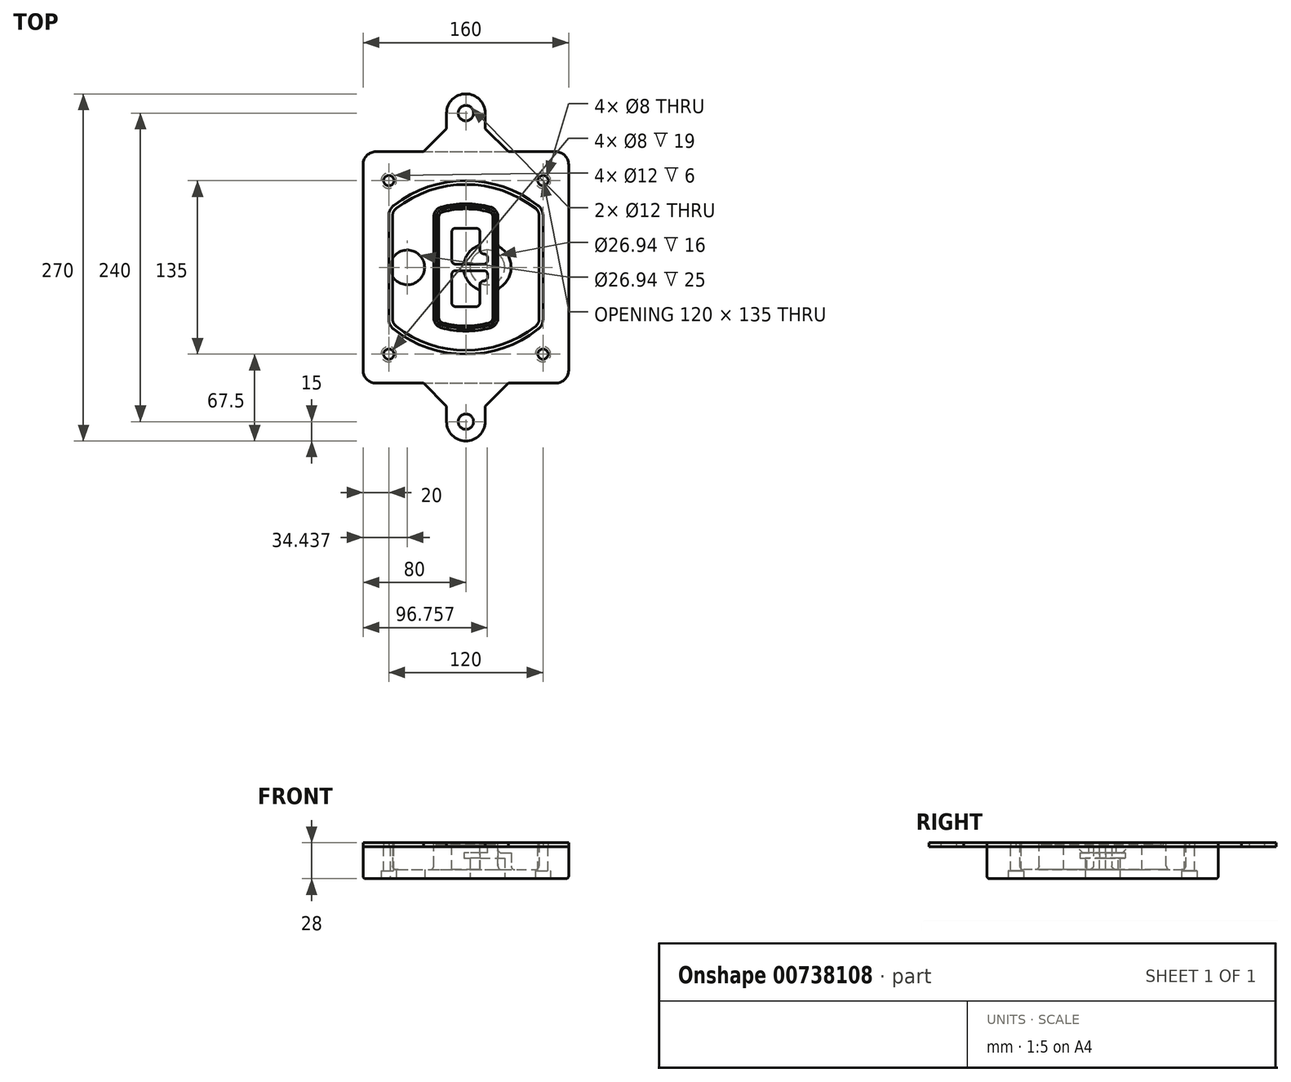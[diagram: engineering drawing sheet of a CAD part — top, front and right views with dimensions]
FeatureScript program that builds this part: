
annotation { "Feature Type Name" : "Feature", "Feature Type Description" : "" }
export const myFeature = defineFeature(function(context is Context, id is Id, definition is map)
    precondition{}
    {
        {
            var Q0;
            Q0=qCreatedBy(makeId("Top.planeOp"),FACE);
            var sketch = newSketch(context, id + "F0", { "sketchPlane" : qUnion([Q0])});
            skPoint(sketch, "E0.rect.middle", {"position": v(0, 0) * mm});
            skLineSegment(sketch, "E1.bottom", {"start": v(-70, -90) * mm, "end": v(70, -90) * mm});
            skLineSegment(sketch, "E1.top", {"start": v(-70, 90) * mm, "end": v(70, 90) * mm});
            skLineSegment(sketch, "E1.left", {"start": v(-80, -80) * mm, "end": v(-80, 80) * mm});
            skLineSegment(sketch, "E1.right", {"start": v(80, -80) * mm, "end": v(80, 80) * mm});
            skLineSegment(sketch, "E2", {"start": v(-80, 90) * mm, "end": v(80, -90) * mm, "construction": true});
            skLineSegment(sketch, "E3", {"start": v(80, 90) * mm, "end": v(-80, -90) * mm, "construction": true});
            skCircle(sketch, "E4", {"center": v(-60, 67.5) * mm, "radius": 4 * mm});
            skCircle(sketch, "E5", {"center": v(60, 67.5) * mm, "radius": 4 * mm});
            skCircle(sketch, "E6", {"center": v(60, -67.5) * mm, "radius": 4 * mm});
            skCircle(sketch, "E7", {"center": v(-60, -67.5) * mm, "radius": 4 * mm});
            skLineSegment(sketch, "E8", {"start": v(-60, 67.5) * mm, "end": v(60, 67.5) * mm, "construction": true});
            skLineSegment(sketch, "E9", {"start": v(60, 67.5) * mm, "end": v(60, -67.5) * mm, "construction": true});
            skLineSegment(sketch, "E10", {"start": v(60, -67.5) * mm, "end": v(-60, -67.5) * mm, "construction": true});
            skLineSegment(sketch, "E11", {"start": v(-60, -67.5) * mm, "end": v(-60, 67.5) * mm, "construction": true});
            skLineSegment(sketch, "E12", {"start": v(-60, 40.3) * mm, "end": v(-60, -40.3) * mm});
            skLineSegment(sketch, "E13", {"start": v(60, 40.3) * mm, "end": v(60, -40.3) * mm});
            skArc(sketch, "E14", {"start": v(56.15, 48.18) * mm, "mid": v(0, 67.5) * mm, "end": v(-56.15, 48.18) * mm});
            skArc(sketch, "E15", {"start": v(-56.15, -48.18) * mm, "mid": v(0, -67.5) * mm, "end": v(56.15, -48.18) * mm});
            skLineSegment(sketch, "E16", {"start": v(-60, 0) * mm, "end": v(60, 0) * mm, "construction": true});
            skPoint(sketch, "E17.visualSharp", {"position": v(-60, -45) * mm});
            skArc(sketch, "E17.filletArc", {"start": v(-60, -40.3) * mm, "mid": v(-58.99, -44.68) * mm, "end": v(-56.15, -48.18) * mm});
            skPoint(sketch, "E18.visualSharp", {"position": v(-60, 45) * mm});
            skArc(sketch, "E18.filletArc", {"start": v(-56.15, 48.18) * mm, "mid": v(-58.99, 44.68) * mm, "end": v(-60, 40.3) * mm});
            skPoint(sketch, "E19.visualSharp", {"position": v(60, 45) * mm});
            skArc(sketch, "E19.filletArc", {"start": v(60, 40.3) * mm, "mid": v(58.99, 44.68) * mm, "end": v(56.15, 48.18) * mm});
            skPoint(sketch, "E20.visualSharp", {"position": v(60, -45) * mm});
            skArc(sketch, "E20.filletArc", {"start": v(56.15, -48.18) * mm, "mid": v(58.99, -44.68) * mm, "end": v(60, -40.3) * mm});
            skPoint(sketch, "E21.visualSharp", {"position": v(-80, 90) * mm});
            skArc(sketch, "E21.filletArc", {"start": v(-70, 90) * mm, "mid": v(-77.07, 87.07) * mm, "end": v(-80, 80) * mm});
            skPoint(sketch, "E22.visualSharp", {"position": v(80, 90) * mm});
            skArc(sketch, "E22.filletArc", {"start": v(80, 80) * mm, "mid": v(77.07, 87.07) * mm, "end": v(70, 90) * mm});
            skPoint(sketch, "E23.visualSharp", {"position": v(80, -90) * mm});
            skArc(sketch, "E23.filletArc", {"start": v(70, -90) * mm, "mid": v(77.07, -87.07) * mm, "end": v(80, -80) * mm});
            skPoint(sketch, "E24.visualSharp", {"position": v(-80, -90) * mm});
            skArc(sketch, "E24.filletArc", {"start": v(-80, -80) * mm, "mid": v(-77.07, -87.07) * mm, "end": v(-70, -90) * mm});
            skArc(sketch, "E25.0", {"start": v(57, 40.3) * mm, "mid": v(56.3, 43.36) * mm, "end": v(54.3, 45.81) * mm});
            skLineSegment(sketch, "E25.1", {"start": v(57, 40.3) * mm, "end": v(57, -40.3) * mm});
            skArc(sketch, "E25.2", {"start": v(54.3, -45.81) * mm, "mid": v(56.3, -43.36) * mm, "end": v(57, -40.3) * mm});
            skArc(sketch, "E25.3", {"start": v(-54.3, -45.81) * mm, "mid": v(0, -64.5) * mm, "end": v(54.3, -45.81) * mm});
            skArc(sketch, "E25.4", {"start": v(-57, -40.3) * mm, "mid": v(-56.3, -43.36) * mm, "end": v(-54.3, -45.81) * mm});
            skArc(sketch, "E25.5", {"start": v(54.3, 45.81) * mm, "mid": v(0, 64.5) * mm, "end": v(-54.3, 45.81) * mm});
            skLineSegment(sketch, "E25.6", {"start": v(-57, 40.3) * mm, "end": v(-57, -40.3) * mm});
            skArc(sketch, "E25.7", {"start": v(-54.3, 45.81) * mm, "mid": v(-56.3, 43.36) * mm, "end": v(-57, 40.3) * mm});
            skArc(sketch, "E26.0", {"start": v(-58.62, 51.33) * mm, "mid": v(-62.58, 46.43) * mm, "end": v(-64, 40.3) * mm});
            skArc(sketch, "E26.1", {"start": v(58.62, 51.33) * mm, "mid": v(0, 71.5) * mm, "end": v(-58.62, 51.33) * mm});
            skArc(sketch, "E26.2", {"start": v(64, 40.3) * mm, "mid": v(62.58, 46.43) * mm, "end": v(58.62, 51.33) * mm});
            skLineSegment(sketch, "E26.3", {"start": v(64, 40.3) * mm, "end": v(64, -40.3) * mm});
            skArc(sketch, "E26.4", {"start": v(58.62, -51.33) * mm, "mid": v(62.58, -46.43) * mm, "end": v(64, -40.3) * mm});
            skLineSegment(sketch, "E26.5", {"start": v(-64, 40.3) * mm, "end": v(-64, -40.3) * mm});
            skArc(sketch, "E26.6", {"start": v(-58.62, -51.33) * mm, "mid": v(0, -71.5) * mm, "end": v(58.62, -51.33) * mm});
            skArc(sketch, "E26.7", {"start": v(-64, -40.3) * mm, "mid": v(-62.58, -46.43) * mm, "end": v(-58.62, -51.33) * mm});
            skSolve(sketch);
        }
        {
            var Q0;
            Q0=makeQuery(id+"F0.imprint","IMPRINT",FACE,{"disambiguationData":[TD([[makeQuery(id+"F0.imprint","IMPRINT",EDGE,{"derivedFrom":sQuery(id+"F0.wireOp",EDGE,"E1.bottom")}),1.0]])]});
            var Q1;
            Q1=makeQuery(id+"F0.imprint","IMPRINT",FACE,{"disambiguationData":[TD([[makeQuery(id+"F0.imprint","IMPRINT",EDGE,{"derivedFrom":sQuery(id+"F0.wireOp",EDGE,"E12")}),1.0]])]});
            var Q2;
            Q2=makeQuery(id+"F0.imprint","IMPRINT",FACE,{"disambiguationData":[TD([[makeQuery(id+"F0.imprint","IMPRINT",EDGE,{"derivedFrom":sQuery(id+"F0.wireOp",EDGE,"E25.0")}),1.0]])]});
            var Q3;
            Q3=makeQuery(id+"F0.imprint","IMPRINT",FACE,{"disambiguationData":[TD([[makeQuery(id+"F0.imprint","IMPRINT",EDGE,{"derivedFrom":sQuery(id+"F0.wireOp",EDGE,"E12")}),-1.0]])]});
            extrude(context, id + "F1", {"entities" : qUnion([Q0, Q1, Q2, Q3]), "oppositeDirection" : true, "depth" : 25 * mm});
        }
        {
            var Q0;
            Q0=makeQuery(id+"F0.imprint","IMPRINT",FACE,{"disambiguationData":[TD([[makeQuery(id+"F0.imprint","IMPRINT",EDGE,{"derivedFrom":sQuery(id+"F0.wireOp",EDGE,"E12")}),1.0]])]});
            extrude(context, id + "F2", {"entities" : qUnion([Q0]), "operationType" : NewBodyOperationType.ADD, "depth" : 3 * mm});
        }
        {
            var Q0;
            Q0=makeQuery(id+"F0.imprint","IMPRINT",FACE,{"disambiguationData":[TD([[makeQuery(id+"F0.imprint","IMPRINT",EDGE,{"derivedFrom":sQuery(id+"F0.wireOp",EDGE,"E25.0")}),1.0]])]});
            extrude(context, id + "F3", {"entities" : qUnion([Q0]), "operationType" : NewBodyOperationType.REMOVE, "oppositeDirection" : true, "depth" : 18 * mm});
        }
        {
            var Q0;
            Q0=makeQuery(id+"F2.opExtrude","CAP_FACE",FACE,{"disambiguationData":[OSD([sQuery(id+"F0.wireOp",EDGE,"E12"),sQuery(id+"F0.wireOp",EDGE,"E13"),sQuery(id+"F0.wireOp",EDGE,"E14"),sQuery(id+"F0.wireOp",EDGE,"E15"),sQuery(id+"F0.wireOp",EDGE,"E17.filletArc"),sQuery(id+"F0.wireOp",EDGE,"E18.filletArc"),sQuery(id+"F0.wireOp",EDGE,"E19.filletArc"),sQuery(id+"F0.wireOp",EDGE,"E20.filletArc"),sQuery(id+"F0.wireOp",EDGE,"E25.0"),sQuery(id+"F0.wireOp",EDGE,"E25.1"),sQuery(id+"F0.wireOp",EDGE,"E25.2"),sQuery(id+"F0.wireOp",EDGE,"E25.3"),sQuery(id+"F0.wireOp",EDGE,"E25.4"),sQuery(id+"F0.wireOp",EDGE,"E25.5"),sQuery(id+"F0.wireOp",EDGE,"E25.6"),sQuery(id+"F0.wireOp",EDGE,"E25.7")])],"isStart":false});
            var sketch = newSketch(context, id + "F4", { "sketchPlane" : qUnion([Q0])});
            skArc(sketch, "E27.0", {"start": v(-19.08, -46.97) * mm, "mid": v(0, -49.5) * mm, "end": v(19.08, -46.97) * mm});
            skArc(sketch, "E28.0", {"start": v(19.08, 46.97) * mm, "mid": v(0, 49.5) * mm, "end": v(-19.08, 46.97) * mm});
            skLineSegment(sketch, "E29", {"start": v(-25, 39.25) * mm, "end": v(-25, -39.25) * mm});
            skLineSegment(sketch, "E30", {"start": v(25, 39.25) * mm, "end": v(25, -39.25) * mm});
            skLineSegment(sketch, "E31", {"start": v(-25, 45.1) * mm, "end": v(25, 45.1) * mm, "construction": true});
            skLineSegment(sketch, "E32", {"start": v(-25, -45.1) * mm, "end": v(25, -45.1) * mm, "construction": true});
            skPoint(sketch, "E33.visualSharp", {"position": v(-25, 45.1) * mm});
            skArc(sketch, "E33.filletArc", {"start": v(-19.08, 46.97) * mm, "mid": v(-23.35, 44.11) * mm, "end": v(-25, 39.25) * mm});
            skPoint(sketch, "E34.visualSharp", {"position": v(25, 45.1) * mm});
            skArc(sketch, "E34.filletArc", {"start": v(25, 39.25) * mm, "mid": v(23.35, 44.11) * mm, "end": v(19.08, 46.97) * mm});
            skPoint(sketch, "E35.visualSharp", {"position": v(25, -45.1) * mm});
            skArc(sketch, "E35.filletArc", {"start": v(19.08, -46.97) * mm, "mid": v(23.35, -44.11) * mm, "end": v(25, -39.25) * mm});
            skPoint(sketch, "E36.visualSharp", {"position": v(-25, -45.1) * mm});
            skArc(sketch, "E36.filletArc", {"start": v(-25, -39.25) * mm, "mid": v(-23.35, -44.11) * mm, "end": v(-19.08, -46.97) * mm});
            skArc(sketch, "E37.0", {"start": v(54.3, 45.81) * mm, "mid": v(0, 64.5) * mm, "end": v(-54.3, 45.81) * mm});
            skArc(sketch, "E37.1", {"start": v(-54.3, 45.81) * mm, "mid": v(-56.3, 43.36) * mm, "end": v(-57, 40.3) * mm});
            skLineSegment(sketch, "E37.2", {"start": v(-57, 40.3) * mm, "end": v(-57, -40.3) * mm});
            skArc(sketch, "E37.3", {"start": v(-57, -40.3) * mm, "mid": v(-56.3, -43.36) * mm, "end": v(-54.3, -45.81) * mm});
            skArc(sketch, "E37.4", {"start": v(-54.3, -45.81) * mm, "mid": v(0, -64.5) * mm, "end": v(54.3, -45.81) * mm});
            skArc(sketch, "E37.5", {"start": v(54.3, -45.81) * mm, "mid": v(56.3, -43.36) * mm, "end": v(57, -40.3) * mm});
            skLineSegment(sketch, "E37.6", {"start": v(57, 40.3) * mm, "end": v(57, -40.3) * mm});
            skArc(sketch, "E37.7", {"start": v(57, 40.3) * mm, "mid": v(56.3, 43.36) * mm, "end": v(54.3, 45.81) * mm});
            skLineSegment(sketch, "E38.0", {"start": v(23, 39.25) * mm, "end": v(23, -39.25) * mm});
            skArc(sketch, "E38.1", {"start": v(18.56, -45.04) * mm, "mid": v(21.76, -42.9) * mm, "end": v(23, -39.25) * mm});
            skArc(sketch, "E38.2", {"start": v(-18.56, -45.04) * mm, "mid": v(0, -47.5) * mm, "end": v(18.56, -45.04) * mm});
            skArc(sketch, "E38.3", {"start": v(-23, -39.25) * mm, "mid": v(-21.76, -42.9) * mm, "end": v(-18.56, -45.04) * mm});
            skLineSegment(sketch, "E38.4", {"start": v(-23, 39.25) * mm, "end": v(-23, -39.25) * mm});
            skArc(sketch, "E38.5", {"start": v(23, 39.25) * mm, "mid": v(21.76, 42.9) * mm, "end": v(18.56, 45.04) * mm});
            skArc(sketch, "E38.6", {"start": v(-18.56, 45.04) * mm, "mid": v(-21.76, 42.9) * mm, "end": v(-23, 39.25) * mm});
            skArc(sketch, "E38.7", {"start": v(18.56, 45.04) * mm, "mid": v(0, 47.5) * mm, "end": v(-18.56, 45.04) * mm});
            skArc(sketch, "E39.0", {"start": v(21, 39.25) * mm, "mid": v(20.18, 41.68) * mm, "end": v(18.04, 43.1) * mm});
            skLineSegment(sketch, "E39.1", {"start": v(21, 39.25) * mm, "end": v(21, -39.25) * mm});
            skArc(sketch, "E39.2", {"start": v(18.04, -43.1) * mm, "mid": v(20.18, -41.68) * mm, "end": v(21, -39.25) * mm});
            skArc(sketch, "E39.3", {"start": v(-18.04, -43.1) * mm, "mid": v(0, -45.5) * mm, "end": v(18.04, -43.1) * mm});
            skArc(sketch, "E39.4", {"start": v(-21, -39.25) * mm, "mid": v(-20.18, -41.68) * mm, "end": v(-18.04, -43.1) * mm});
            skArc(sketch, "E39.5", {"start": v(18.04, 43.1) * mm, "mid": v(0, 45.5) * mm, "end": v(-18.04, 43.1) * mm});
            skLineSegment(sketch, "E39.6", {"start": v(-21, 39.25) * mm, "end": v(-21, -39.25) * mm});
            skArc(sketch, "E39.7", {"start": v(-18.04, 43.1) * mm, "mid": v(-20.18, 41.68) * mm, "end": v(-21, 39.25) * mm});
            skLineSegment(sketch, "E40", {"start": v(-25, 0) * mm, "end": v(25, 0) * mm, "construction": true});
            skLineSegment(sketch, "E41", {"start": v(-11, 5.5) * mm, "end": v(-11, 27.5) * mm});
            skLineSegment(sketch, "E42", {"start": v(-8, 30.5) * mm, "end": v(8, 30.5) * mm});
            skLineSegment(sketch, "E43", {"start": v(11, 27.5) * mm, "end": v(11, 13.5) * mm});
            skLineSegment(sketch, "E44", {"start": v(14, 10.5) * mm, "end": v(14, 10.5) * mm});
            skLineSegment(sketch, "E45", {"start": v(17, 7.5) * mm, "end": v(17, 5.5) * mm});
            skLineSegment(sketch, "E46", {"start": v(14, 2.5) * mm, "end": v(-8, 2.5) * mm});
            skPoint(sketch, "E47.visualSharp", {"position": v(-11, 30.5) * mm});
            skArc(sketch, "E47.filletArc", {"start": v(-8, 30.5) * mm, "mid": v(-10.12, 29.62) * mm, "end": v(-11, 27.5) * mm});
            skPoint(sketch, "E48.visualSharp", {"position": v(11, 30.5) * mm});
            skArc(sketch, "E48.filletArc", {"start": v(11, 27.5) * mm, "mid": v(10.12, 29.62) * mm, "end": v(8, 30.5) * mm});
            skPoint(sketch, "E49.visualSharp", {"position": v(11, 10.5) * mm});
            skArc(sketch, "E49.filletArc", {"start": v(11, 13.5) * mm, "mid": v(11.88, 11.38) * mm, "end": v(14, 10.5) * mm});
            skPoint(sketch, "E50.visualSharp", {"position": v(17, 10.5) * mm});
            skArc(sketch, "E50.filletArc", {"start": v(17, 7.5) * mm, "mid": v(16.12, 9.62) * mm, "end": v(14, 10.5) * mm});
            skPoint(sketch, "E51.visualSharp", {"position": v(17, 2.5) * mm});
            skArc(sketch, "E51.filletArc", {"start": v(14, 2.5) * mm, "mid": v(16.12, 3.38) * mm, "end": v(17, 5.5) * mm});
            skPoint(sketch, "E52.visualSharp", {"position": v(-11, 2.5) * mm});
            skArc(sketch, "E52.filletArc", {"start": v(-11, 5.5) * mm, "mid": v(-10.12, 3.38) * mm, "end": v(-8, 2.5) * mm});
            skLineSegment(sketch, "E53.0.MirrorCS", {"start": v(14, -2.5) * mm, "end": v(-8, -2.5) * mm});
            skArc(sketch, "E54.0.MirrorCS", {"start": v(-11, -5.5) * mm, "mid": v(-10.12, -3.38) * mm, "end": v(-8, -2.5) * mm});
            skLineSegment(sketch, "E55.0.MirrorCS", {"start": v(-11, -5.5) * mm, "end": v(-11, -27.5) * mm});
            skArc(sketch, "E56.0.MirrorCS", {"start": v(-8, -30.5) * mm, "mid": v(-10.12, -29.62) * mm, "end": v(-11, -27.5) * mm});
            skLineSegment(sketch, "E57.0.MirrorCS", {"start": v(-8, -30.5) * mm, "end": v(8, -30.5) * mm});
            skArc(sketch, "E58.0.MirrorCS", {"start": v(11, -27.5) * mm, "mid": v(10.12, -29.62) * mm, "end": v(8, -30.5) * mm});
            skLineSegment(sketch, "E59.0.MirrorCS", {"start": v(11, -27.5) * mm, "end": v(11, -13.5) * mm});
            skArc(sketch, "E60.0.MirrorCS", {"start": v(11, -13.5) * mm, "mid": v(11.88, -11.38) * mm, "end": v(14, -10.5) * mm});
            skArc(sketch, "E61.0.MirrorCS", {"start": v(17, -7.5) * mm, "mid": v(16.12, -9.62) * mm, "end": v(14, -10.5) * mm});
            skLineSegment(sketch, "E62.0.MirrorCS", {"start": v(17, -7.5) * mm, "end": v(17, -5.5) * mm});
            skArc(sketch, "E63.0.MirrorCS", {"start": v(14, -2.5) * mm, "mid": v(16.12, -3.38) * mm, "end": v(17, -5.5) * mm});
            skSolve(sketch);
        }
        {
            var Q0;
            Q0=makeQuery(id+"F4.imprint","IMPRINT",FACE,{"disambiguationData":[TD([[makeQuery(id+"F4.imprint","IMPRINT",EDGE,{"derivedFrom":sQuery(id+"F4.wireOp",EDGE,"E27.0")}),1.0]])]});
            var Q1;
            Q1=makeQuery(id+"F4.imprint","IMPRINT",FACE,{"disambiguationData":[TD([[makeQuery(id+"F4.imprint","IMPRINT",EDGE,{"derivedFrom":sQuery(id+"F4.wireOp",EDGE,"E38.0")}),-1.0]])]});
            var Q2;
            Q2=makeQuery(id+"F4.imprint","IMPRINT",FACE,{"disambiguationData":[TD([[makeQuery(id+"F4.imprint","IMPRINT",EDGE,{"derivedFrom":sQuery(id+"F4.wireOp",EDGE,"E39.0")}),1.0]])]});
            extrude(context, id + "F5", {"entities" : qUnion([Q0, Q1, Q2]), "operationType" : NewBodyOperationType.ADD, "endBound" : BoundingType.UP_TO_NEXT, "oppositeDirection" : true, "depth" : 25 * mm});
        }
        {
            var Q0;
            Q0=makeQuery(id+"F4.imprint","IMPRINT",FACE,{"disambiguationData":[TD([[makeQuery(id+"F4.imprint","IMPRINT",EDGE,{"derivedFrom":sQuery(id+"F4.wireOp",EDGE,"E38.0")}),-1.0]])]});
            extrude(context, id + "F6", {"entities" : qUnion([Q0]), "operationType" : NewBodyOperationType.REMOVE, "oppositeDirection" : true, "depth" : 2 * mm});
        }
        {
            var Q0;
            Q0=makeQuery(id+"F1.opExtrude","CAP_FACE",FACE,{"disambiguationData":[OSD([sQuery(id+"F0.wireOp",EDGE,"E1.bottom"),sQuery(id+"F0.wireOp",EDGE,"E1.top"),sQuery(id+"F0.wireOp",EDGE,"E1.left"),sQuery(id+"F0.wireOp",EDGE,"E1.right"),sQuery(id+"F0.wireOp",EDGE,"E4"),sQuery(id+"F0.wireOp",EDGE,"E5"),sQuery(id+"F0.wireOp",EDGE,"E6"),sQuery(id+"F0.wireOp",EDGE,"E7"),sQuery(id+"F0.wireOp",EDGE,"E21.filletArc"),sQuery(id+"F0.wireOp",EDGE,"E22.filletArc"),sQuery(id+"F0.wireOp",EDGE,"E23.filletArc"),sQuery(id+"F0.wireOp",EDGE,"E24.filletArc")])],"isStart":false});
            var sketch = newSketch(context, id + "F7", { "sketchPlane" : qUnion([Q0])});
            skCircle(sketch, "E64", {"center": v(16.76, 0) * mm, "radius": 13.47 * mm});
            skCircle(sketch, "E65", {"center": v(-45.56, 0) * mm, "radius": 13.47 * mm});
            skLineSegment(sketch, "E66", {"start": v(80, 0) * mm, "end": v(-80, 0) * mm});
            skCircle(sketch, "E67", {"center": v(16.76, 0) * mm, "radius": 18.47 * mm});
            skCircle(sketch, "E68", {"center": v(60, -67.5) * mm, "radius": 6 * mm});
            skCircle(sketch, "E69", {"center": v(-60, -67.5) * mm, "radius": 6 * mm});
            skCircle(sketch, "E70", {"center": v(-60, 67.5) * mm, "radius": 6 * mm});
            skCircle(sketch, "E71", {"center": v(60, 67.5) * mm, "radius": 6 * mm});
            skSolve(sketch);
        }
        {
            var Q0;
            {var subQ1=sQuery(id+"F7.wireOp",EDGE,"E66");var subQ4=sQuery(id+"F7.wireOp",EDGE,"E64");var subQ6=makeQuery(id+"F7.imprint","INTERSECT",VERTEX,{"disambiguationData":[OD(0.0)],"derivedFrom":[subQ4,subQ1]});Q0=makeQuery(id+"F7.imprint","IMPRINT",FACE,{"disambiguationData":[TD([[makeQuery(id+"F7.imprint","IMPRINT",EDGE,{"disambiguationData":[TD([[subQ6,-1.0]])],"derivedFrom":subQ4}),-1.0]])]});}
            var Q1;
            {var subQ0=sQuery(id+"F7.wireOp",EDGE,"E66");var subQ1=sQuery(id+"F7.wireOp",EDGE,"E64");var subQ3=makeQuery(id+"F7.imprint","INTERSECT",VERTEX,{"disambiguationData":[OD(0.0)],"derivedFrom":[subQ1,subQ0]});Q1=makeQuery(id+"F7.imprint","IMPRINT",FACE,{"disambiguationData":[TD([[makeQuery(id+"F7.imprint","IMPRINT",EDGE,{"disambiguationData":[TD([[subQ3,-1.0]])],"derivedFrom":subQ1}),1.0]])]});}
            var Q2;
            {var subQ0=sQuery(id+"F7.wireOp",EDGE,"E66");var subQ1=sQuery(id+"F7.wireOp",EDGE,"E64");var subQ3=makeQuery(id+"F7.imprint","INTERSECT",VERTEX,{"disambiguationData":[OD(0.0)],"derivedFrom":[subQ1,subQ0]});Q2=makeQuery(id+"F7.imprint","IMPRINT",FACE,{"disambiguationData":[TD([[makeQuery(id+"F7.imprint","IMPRINT",EDGE,{"disambiguationData":[TD([[subQ3,1.0]])],"derivedFrom":subQ1}),1.0]])]});}
            var Q3;
            {var subQ1=sQuery(id+"F7.wireOp",EDGE,"E66");var subQ4=sQuery(id+"F7.wireOp",EDGE,"E64");var subQ6=makeQuery(id+"F7.imprint","INTERSECT",VERTEX,{"disambiguationData":[OD(0.0)],"derivedFrom":[subQ4,subQ1]});Q3=makeQuery(id+"F7.imprint","IMPRINT",FACE,{"disambiguationData":[TD([[makeQuery(id+"F7.imprint","IMPRINT",EDGE,{"disambiguationData":[TD([[subQ6,1.0]])],"derivedFrom":subQ4}),-1.0]])]});}
            extrude(context, id + "F8", {"entities" : qUnion([Q0, Q1, Q2, Q3]), "operationType" : NewBodyOperationType.ADD, "oppositeDirection" : true, "depth" : 20 * mm});
        }
        {
            var Q0;
            {var subQ0=sQuery(id+"F7.wireOp",EDGE,"E66");var subQ1=sQuery(id+"F7.wireOp",EDGE,"E64");var subQ3=makeQuery(id+"F7.imprint","INTERSECT",VERTEX,{"disambiguationData":[OD(0.0)],"derivedFrom":[subQ1,subQ0]});Q0=makeQuery(id+"F7.imprint","IMPRINT",FACE,{"disambiguationData":[TD([[makeQuery(id+"F7.imprint","IMPRINT",EDGE,{"disambiguationData":[TD([[subQ3,-1.0]])],"derivedFrom":subQ1}),1.0]])]});}
            var Q1;
            {var subQ0=sQuery(id+"F7.wireOp",EDGE,"E66");var subQ1=sQuery(id+"F7.wireOp",EDGE,"E64");var subQ3=makeQuery(id+"F7.imprint","INTERSECT",VERTEX,{"disambiguationData":[OD(0.0)],"derivedFrom":[subQ1,subQ0]});Q1=makeQuery(id+"F7.imprint","IMPRINT",FACE,{"disambiguationData":[TD([[makeQuery(id+"F7.imprint","IMPRINT",EDGE,{"disambiguationData":[TD([[subQ3,1.0]])],"derivedFrom":subQ1}),1.0]])]});}
            extrude(context, id + "F9", {"entities" : qUnion([Q0, Q1]), "operationType" : NewBodyOperationType.REMOVE, "oppositeDirection" : true, "depth" : 16 * mm});
        }
        {
            var Q0;
            {var subQ0=sQuery(id+"F7.wireOp",EDGE,"E66");var subQ1=sQuery(id+"F7.wireOp",EDGE,"E65");var subQ3=makeQuery(id+"F7.imprint","INTERSECT",VERTEX,{"disambiguationData":[OD(0.0)],"derivedFrom":[subQ1,subQ0]});Q0=makeQuery(id+"F7.imprint","IMPRINT",FACE,{"disambiguationData":[TD([[makeQuery(id+"F7.imprint","IMPRINT",EDGE,{"disambiguationData":[TD([[subQ3,-1.0]])],"derivedFrom":subQ1}),1.0]])]});}
            var Q1;
            {var subQ0=sQuery(id+"F7.wireOp",EDGE,"E66");var subQ1=sQuery(id+"F7.wireOp",EDGE,"E65");var subQ3=makeQuery(id+"F7.imprint","INTERSECT",VERTEX,{"disambiguationData":[OD(0.0)],"derivedFrom":[subQ1,subQ0]});Q1=makeQuery(id+"F7.imprint","IMPRINT",FACE,{"disambiguationData":[TD([[makeQuery(id+"F7.imprint","IMPRINT",EDGE,{"disambiguationData":[TD([[subQ3,1.0]])],"derivedFrom":subQ1}),1.0]])]});}
            extrude(context, id + "F10", {"entities" : qUnion([Q0, Q1]), "operationType" : NewBodyOperationType.REMOVE, "oppositeDirection" : true, "depth" : 25 * mm});
        }
        {
            var Q0;
            Q0=makeQuery(id+"F7.imprint","IMPRINT",FACE,{"disambiguationData":[TD([[makeQuery(id+"F7.imprint","IMPRINT",EDGE,{"derivedFrom":sQuery(id+"F7.wireOp",EDGE,"E68")}),1.0]])]});
            var Q1;
            Q1=makeQuery(id+"F7.imprint","IMPRINT",FACE,{"disambiguationData":[TD([[makeQuery(id+"F7.imprint","IMPRINT",EDGE,{"derivedFrom":makeQuery(id+"F1.opExtrude","CAP_EDGE",EDGE,{"disambiguationData":[OSD([sQuery(id+"F0.wireOp",EDGE,"E5")])],"isStart":false})}),-1.0]])]});
            var Q2;
            Q2=makeQuery(id+"F7.imprint","IMPRINT",FACE,{"disambiguationData":[TD([[makeQuery(id+"F7.imprint","IMPRINT",EDGE,{"derivedFrom":sQuery(id+"F7.wireOp",EDGE,"E69")}),1.0]])]});
            var Q3;
            Q3=makeQuery(id+"F7.imprint","IMPRINT",FACE,{"disambiguationData":[TD([[makeQuery(id+"F7.imprint","IMPRINT",EDGE,{"derivedFrom":makeQuery(id+"F1.opExtrude","CAP_EDGE",EDGE,{"disambiguationData":[OSD([sQuery(id+"F0.wireOp",EDGE,"E4")])],"isStart":false})}),-1.0]])]});
            var Q4;
            Q4=makeQuery(id+"F7.imprint","IMPRINT",FACE,{"disambiguationData":[TD([[makeQuery(id+"F7.imprint","IMPRINT",EDGE,{"derivedFrom":sQuery(id+"F7.wireOp",EDGE,"E70")}),1.0]])]});
            var Q5;
            Q5=makeQuery(id+"F7.imprint","IMPRINT",FACE,{"disambiguationData":[TD([[makeQuery(id+"F7.imprint","IMPRINT",EDGE,{"derivedFrom":makeQuery(id+"F1.opExtrude","CAP_EDGE",EDGE,{"disambiguationData":[OSD([sQuery(id+"F0.wireOp",EDGE,"E7")])],"isStart":false})}),-1.0]])]});
            var Q6;
            Q6=makeQuery(id+"F7.imprint","IMPRINT",FACE,{"disambiguationData":[TD([[makeQuery(id+"F7.imprint","IMPRINT",EDGE,{"derivedFrom":sQuery(id+"F7.wireOp",EDGE,"E71")}),1.0]])]});
            var Q7;
            Q7=makeQuery(id+"F7.imprint","IMPRINT",FACE,{"disambiguationData":[TD([[makeQuery(id+"F7.imprint","IMPRINT",EDGE,{"derivedFrom":makeQuery(id+"F1.opExtrude","CAP_EDGE",EDGE,{"disambiguationData":[OSD([sQuery(id+"F0.wireOp",EDGE,"E6")])],"isStart":false})}),-1.0]])]});
            extrude(context, id + "F11", {"entities" : qUnion([Q0, Q1, Q2, Q3, Q4, Q5, Q6, Q7]), "operationType" : NewBodyOperationType.REMOVE, "oppositeDirection" : true, "depth" : 6 * mm});
        }
        {
            var Q0;
            Q0=makeQuery(id+"F9.boolean.opBoolean","COPY",FACE,{"derivedFrom":makeQuery(id+"F9.opExtrude","CAP_FACE",FACE,{"disambiguationData":[OSD([sQuery(id+"F7.wireOp",EDGE,"E64")])],"isStart":false})});
            var sketch = newSketch(context, id + "F12", { "sketchPlane" : qUnion([Q0])});
            skArc(sketch, "E72.0", {"start": v(11, 17.55) * mm, "mid": v(2.57, 11.82) * mm, "end": v(-1.54, 2.5) * mm});
            skArc(sketch, "E72.1", {"start": v(-1.54, -2.5) * mm, "mid": v(2.57, -11.82) * mm, "end": v(11, -17.55) * mm});
            skLineSegment(sketch, "E73", {"start": v(-1.54, -2.5) * mm, "end": v(14, -2.5) * mm});
            skLineSegment(sketch, "E74.0", {"start": v(14, 2.5) * mm, "end": v(-1.54, 2.5) * mm});
            skArc(sketch, "E74.1", {"start": v(14, 2.5) * mm, "mid": v(16.12, 3.38) * mm, "end": v(17, 5.5) * mm});
            skLineSegment(sketch, "E74.2", {"start": v(17, 7.5) * mm, "end": v(17, 5.5) * mm});
            skArc(sketch, "E74.3", {"start": v(17, 7.5) * mm, "mid": v(16.12, 9.62) * mm, "end": v(14, 10.5) * mm});
            skArc(sketch, "E74.4", {"start": v(11, 13.5) * mm, "mid": v(11.88, 11.38) * mm, "end": v(14, 10.5) * mm});
            skLineSegment(sketch, "E74.5", {"start": v(11, 17.55) * mm, "end": v(11, 13.5) * mm});
            skLineSegment(sketch, "E74.7", {"start": v(14, -2.5) * mm, "end": v(-1.54, -2.5) * mm});
            skArc(sketch, "E74.8", {"start": v(14, -2.5) * mm, "mid": v(16.12, -3.38) * mm, "end": v(17, -5.5) * mm});
            skLineSegment(sketch, "E74.9", {"start": v(17, -7.5) * mm, "end": v(17, -5.5) * mm});
            skArc(sketch, "E74.10", {"start": v(17, -7.5) * mm, "mid": v(16.12, -9.62) * mm, "end": v(14, -10.5) * mm});
            skArc(sketch, "E74.11", {"start": v(11, -13.5) * mm, "mid": v(11.88, -11.38) * mm, "end": v(14, -10.5) * mm});
            skLineSegment(sketch, "E74.12", {"start": v(11, -17.55) * mm, "end": v(11, -13.5) * mm});
            skPoint(sketch, "E75.orphan", {"position": v(11, -27.5) * mm});
            skPoint(sketch, "E76.orphan", {"position": v(-8, -2.5) * mm});
            skPoint(sketch, "E77.orphan", {"position": v(-8, 2.5) * mm});
            skPoint(sketch, "E78.orphan", {"position": v(11, 27.5) * mm});
            skSolve(sketch);
        }
        {
            var Q0;
            {var subQ7=sQuery(id+"F12.wireOp",EDGE,"E72.0");var subQ14=sQuery(id+"F12.wireOp",EDGE,"E72.1");var subQ16=sQuery(id+"F12.wireOp",EDGE,"E74.1");var subQ18=sQuery(id+"F12.wireOp",EDGE,"E74.8");Q0=qUnion([makeQuery(id+"F12.imprint","IMPRINT",FACE,{"disambiguationData":[TD([[makeQuery(id+"F12.imprint","IMPRINT",EDGE,{"derivedFrom":subQ7}),1.0]])]}),makeQuery(id+"F12.imprint","IMPRINT",FACE,{"disambiguationData":[TD([[makeQuery(id+"F12.imprint","IMPRINT",EDGE,{"derivedFrom":subQ14}),1.0]])]}),makeQuery(id+"F12.imprint","IMPRINT",FACE,{"disambiguationData":[TD([[makeQuery(id+"F12.imprint","IMPRINT",EDGE,{"derivedFrom":subQ16}),1.0]])]}),makeQuery(id+"F12.imprint","IMPRINT",FACE,{"disambiguationData":[TD([[makeQuery(id+"F12.imprint","IMPRINT",EDGE,{"derivedFrom":subQ18}),-1.0]])]})]);}
            var Q1;
            Q1=makeQuery(id+"F5.boolean.opBoolean","SPLIT",FACE,{"disambiguationData":[TD([makeQuery(id+"F5.opExtrude","SWEPT_FACE",FACE,{"disambiguationData":[OSD([sQuery(id+"F4.wireOp",EDGE,"E41")])]})])],"derivedFrom":makeQuery(id+"F3.boolean.opBoolean","COPY",FACE,{"derivedFrom":makeQuery(id+"F3.opExtrude","CAP_FACE",FACE,{"disambiguationData":[OSD([sQuery(id+"F0.wireOp",EDGE,"E25.0"),sQuery(id+"F0.wireOp",EDGE,"E25.1"),sQuery(id+"F0.wireOp",EDGE,"E25.2"),sQuery(id+"F0.wireOp",EDGE,"E25.3"),sQuery(id+"F0.wireOp",EDGE,"E25.4"),sQuery(id+"F0.wireOp",EDGE,"E25.5"),sQuery(id+"F0.wireOp",EDGE,"E25.6"),sQuery(id+"F0.wireOp",EDGE,"E25.7")])],"isStart":false})})});
            extrude(context, id + "F13", {"entities" : qUnion([Q0]), "operationType" : NewBodyOperationType.REMOVE, "endBound" : BoundingType.UP_TO_SURFACE, "endBoundEntityFace" : qUnion([Q1]), "depth" : 25 * mm});
        }
        {
            var Q0;
            Q0=makeQuery(id+"F3.boolean.opBoolean","COPY",EDGE,{"derivedFrom":makeQuery(id+"F3.opExtrude","CAP_EDGE",EDGE,{"disambiguationData":[OSD([sQuery(id+"F0.wireOp",EDGE,"E25.6")])],"isStart":false})});
            var Q1;
            Q1=makeQuery(id+"F8.boolean.opBoolean","INTERSECT",EDGE,{"derivedFrom":[makeQuery(id+"F5.opExtrude","SWEPT_FACE",FACE,{"disambiguationData":[OSD([sQuery(id+"F4.wireOp",EDGE,"E30")])]}),makeQuery(id+"F8.opExtrude","CAP_FACE",FACE,{"disambiguationData":[OSD([sQuery(id+"F7.wireOp",EDGE,"E67")])],"isStart":false})]});
            var Q2;
            Q2=makeQuery(id+"F8.boolean.opBoolean","INTERSECT",EDGE,{"disambiguationData":[OD(1.0)],"derivedFrom":[makeQuery(id+"F5.opExtrude","SWEPT_FACE",FACE,{"disambiguationData":[OSD([sQuery(id+"F4.wireOp",EDGE,"E30")])]}),makeQuery(id+"F8.opExtrude","SWEPT_FACE",FACE,{"disambiguationData":[OSD([sQuery(id+"F7.wireOp",EDGE,"E67")])]})]});
            var Q3;
            {var subQ0=sQuery(id+"F4.wireOp",EDGE,"E30");Q3=makeQuery(id+"F8.boolean.opBoolean","SPLIT",EDGE,{"disambiguationData":[TD([makeQuery(id+"F5.opExtrude","SWEPT_FACE",FACE,{"disambiguationData":[OSD([sQuery(id+"F4.wireOp",EDGE,"E35.filletArc")])]})])],"derivedFrom":makeQuery(id+"F5.opExtrude","CAP_EDGE",EDGE,{"disambiguationData":[OSD([subQ0])],"isStart":false})});}
            var Q4;
            {var subQ0=sQuery(id+"F0.wireOp",EDGE,"E25.7");var subQ1=sQuery(id+"F0.wireOp",EDGE,"E25.1");var subQ2=sQuery(id+"F0.wireOp",EDGE,"E25.6");var subQ3=sQuery(id+"F0.wireOp",EDGE,"E25.5");var subQ4=sQuery(id+"F0.wireOp",EDGE,"E25.4");var subQ5=sQuery(id+"F0.wireOp",EDGE,"E25.0");var subQ6=sQuery(id+"F0.wireOp",EDGE,"E25.2");var subQ7=sQuery(id+"F0.wireOp",EDGE,"E25.3");Q4=makeQuery(id+"F8.boolean.opBoolean","INTERSECT",EDGE,{"derivedFrom":[makeQuery(id+"F5.boolean.opBoolean","SPLIT",FACE,{"disambiguationData":[TD([makeQuery(id+"F2.opExtrude","SWEPT_FACE",FACE,{"disambiguationData":[OSD([subQ5])]})])],"derivedFrom":makeQuery(id+"F3.boolean.opBoolean","COPY",FACE,{"derivedFrom":makeQuery(id+"F3.opExtrude","CAP_FACE",FACE,{"disambiguationData":[OSD([subQ5,subQ1,subQ6,subQ7,subQ4,subQ3,subQ2,subQ0])],"isStart":false})})}),makeQuery(id+"F8.opExtrude","SWEPT_FACE",FACE,{"disambiguationData":[OSD([sQuery(id+"F7.wireOp",EDGE,"E67")])]})]});}
            var Q5;
            Q5=makeQuery(id+"F8.boolean.opBoolean","INTERSECT",EDGE,{"disambiguationData":[OD(0.0)],"derivedFrom":[makeQuery(id+"F5.opExtrude","SWEPT_FACE",FACE,{"disambiguationData":[OSD([sQuery(id+"F4.wireOp",EDGE,"E30")])]}),makeQuery(id+"F8.opExtrude","SWEPT_FACE",FACE,{"disambiguationData":[OSD([sQuery(id+"F7.wireOp",EDGE,"E67")])]})]});
            fillet(context, id + "F14", {"entities" : qUnion([Q0, Q1, Q2, Q3, Q4, Q5]), "radius" : 3 * mm, "tangentPropagation" : true, "allowEdgeOverflow" : false});
        }
        {
            var Q0;
            Q0=makeQuery(id+"F1.opExtrude","CAP_EDGE",EDGE,{"disambiguationData":[OSD([sQuery(id+"F0.wireOp",EDGE,"E1.bottom")])],"isStart":false});
            fillet(context, id + "F15", {"entities" : qUnion([Q0]), "radius" : 2 * mm, "tangentPropagation" : true, "allowEdgeOverflow" : false});
        }
        {
            var Q0;
            {var subQ0=sQuery(id+"F0.wireOp",EDGE,"E21.filletArc");var subQ1=sQuery(id+"F0.wireOp",EDGE,"E7");var subQ2=sQuery(id+"F0.wireOp",EDGE,"E6");var subQ3=sQuery(id+"F0.wireOp",EDGE,"E5");var subQ4=sQuery(id+"F0.wireOp",EDGE,"E4");var subQ5=sQuery(id+"F0.wireOp",EDGE,"E22.filletArc");var subQ6=sQuery(id+"F0.wireOp",EDGE,"E1.bottom");var subQ7=sQuery(id+"F0.wireOp",EDGE,"E1.right");var subQ8=sQuery(id+"F0.wireOp",EDGE,"E1.top");var subQ9=sQuery(id+"F0.wireOp",EDGE,"E1.left");var subQ10=sQuery(id+"F0.wireOp",EDGE,"E23.filletArc");var subQ11=sQuery(id+"F0.wireOp",EDGE,"E24.filletArc");Q0=makeQuery(id+"F2.boolean.opBoolean","SPLIT",FACE,{"disambiguationData":[TD([makeQuery(id+"F1.opExtrude","SWEPT_FACE",FACE,{"disambiguationData":[OSD([subQ6])]})])],"derivedFrom":makeQuery(id+"F1.opExtrude","CAP_FACE",FACE,{"disambiguationData":[OSD([subQ6,subQ8,subQ9,subQ7,subQ4,subQ3,subQ2,subQ1,subQ0,subQ5,subQ10,subQ11])],"isStart":true})});}
            var sketch = newSketch(context, id + "F16", { "sketchPlane" : qUnion([Q0])});
            skPoint(sketch, "E79.first.point.positionSnap0", {"position": v(0, 90) * mm});
            skPoint(sketch, "E79.second.point.positionSnap0", {"position": v(0, 90) * mm});
            skLineSegment(sketch, "E80", {"start": v(0, 90) * mm, "end": v(0, 120) * mm, "construction": true});
            skCircle(sketch, "E81", {"center": v(0, 120) * mm, "radius": 6 * mm});
            skLineSegment(sketch, "E82", {"start": v(-33, 90) * mm, "end": v(-15, 108) * mm});
            skLineSegment(sketch, "E83", {"start": v(-15, 108) * mm, "end": v(-15, 120) * mm});
            skLineSegment(sketch, "E84", {"start": v(15, 108) * mm, "end": v(15, 120) * mm});
            skArc(sketch, "E85", {"start": v(15, 120) * mm, "mid": v(0, 135) * mm, "end": v(-15, 120) * mm});
            skLineSegment(sketch, "E86", {"start": v(15, 108) * mm, "end": v(33, 90) * mm});
            skLineSegment(sketch, "E87", {"start": v(-80, 0) * mm, "end": v(80, 0) * mm, "construction": true});
            skArc(sketch, "E88.MirrorCS", {"start": v(15, -120) * mm, "mid": v(0, -135) * mm, "end": v(-15, -120) * mm});
            skLineSegment(sketch, "E89.MirrorCS", {"start": v(15, -108) * mm, "end": v(15, -120) * mm});
            skLineSegment(sketch, "E90.MirrorCS", {"start": v(15, -108) * mm, "end": v(33, -90) * mm});
            skLineSegment(sketch, "E91.MirrorCS", {"start": v(-33, -90) * mm, "end": v(-15, -108) * mm});
            skLineSegment(sketch, "E92.MirrorCS", {"start": v(-15, -108) * mm, "end": v(-15, -120) * mm});
            skCircle(sketch, "E93.MirrorC", {"center": v(0, -120) * mm, "radius": 6 * mm});
            skLineSegment(sketch, "E94.MirrorCS", {"start": v(0, -90) * mm, "end": v(0, -120) * mm, "construction": true});
            skSolve(sketch);
        }
        {
            var Q0;
            Q0=makeQuery(id+"F16.imprint","IMPRINT",FACE,{"disambiguationData":[TD([[makeQuery(id+"F16.imprint","IMPRINT",EDGE,{"derivedFrom":sQuery(id+"F16.wireOp",EDGE,"E81")}),-1.0]])]});
            var Q1;
            Q1=makeQuery(id+"F16.imprint","IMPRINT",FACE,{"disambiguationData":[TD([[makeQuery(id+"F16.imprint","IMPRINT",EDGE,{"derivedFrom":makeQuery(id+"F1.opExtrude","CAP_EDGE",EDGE,{"disambiguationData":[OSD([sQuery(id+"F0.wireOp",EDGE,"E1.left")])],"isStart":true})}),-1.0]])]});
            var Q2;
            Q2=makeQuery(id+"F16.imprint","IMPRINT",FACE,{"disambiguationData":[TD([[makeQuery(id+"F16.imprint","IMPRINT",EDGE,{"derivedFrom":sQuery(id+"F16.wireOp",EDGE,"E89.MirrorCS")}),-1.0]])]});
            var Q3;
            Q3=makeQuery(id+"F2.opExtrude","CAP_FACE",FACE,{"disambiguationData":[OSD([sQuery(id+"F0.wireOp",EDGE,"E12"),sQuery(id+"F0.wireOp",EDGE,"E13"),sQuery(id+"F0.wireOp",EDGE,"E14"),sQuery(id+"F0.wireOp",EDGE,"E15"),sQuery(id+"F0.wireOp",EDGE,"E17.filletArc"),sQuery(id+"F0.wireOp",EDGE,"E18.filletArc"),sQuery(id+"F0.wireOp",EDGE,"E19.filletArc"),sQuery(id+"F0.wireOp",EDGE,"E20.filletArc"),sQuery(id+"F0.wireOp",EDGE,"E25.0"),sQuery(id+"F0.wireOp",EDGE,"E25.1"),sQuery(id+"F0.wireOp",EDGE,"E25.2"),sQuery(id+"F0.wireOp",EDGE,"E25.3"),sQuery(id+"F0.wireOp",EDGE,"E25.4"),sQuery(id+"F0.wireOp",EDGE,"E25.5"),sQuery(id+"F0.wireOp",EDGE,"E25.6"),sQuery(id+"F0.wireOp",EDGE,"E25.7")])],"isStart":false});
            extrude(context, id + "F17", {"entities" : qUnion([Q0, Q1, Q2]), "endBound" : BoundingType.UP_TO_SURFACE, "depth" : 25 * mm, "endBoundEntityFace" : qUnion([Q3]), "offsetDistance" : 25 * mm});
        }
    });
